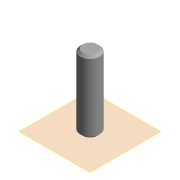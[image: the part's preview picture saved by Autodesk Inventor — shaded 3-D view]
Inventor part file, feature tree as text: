
AUTODESK INVENTOR PART (.ipt)
format: ipt  version: 2014 (Build 180170000, 170)  size: 73,216 bytes
history: native  units: mm
features: plane x1, extrude x1, chamfer x1, sketch x1
ambient origin geometry x8: Origin, YZ Plane, XZ Plane, XY Plane, X Axis, Y Axis, Z Axis, Center Point
bodies: Solid1 (feature_tree)
feature tree (4):
  plane  "Work Plane1"
  extrude  "Extrusion1"  Depth=15.0mm TaperAngle=0.0deg
  chamfer  "Chamfer1"  Distance=2.0mm Angle=45.0deg
  sketch  "Sketch1"  dims[d0=4.0mm d1=15.0mm d2=0.0mm d3=0.5mm d4=2.0mm d5=45.0deg]
